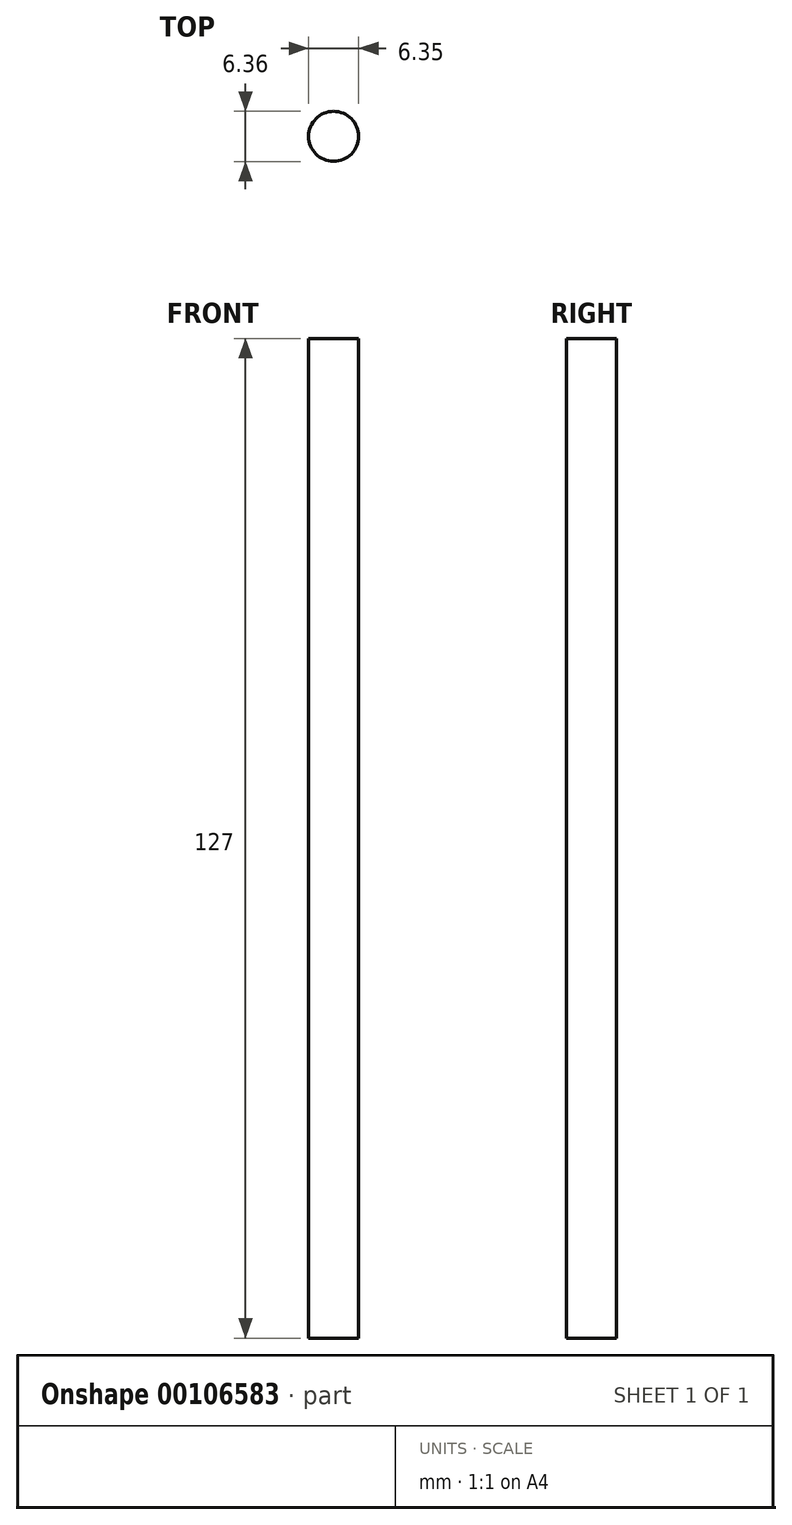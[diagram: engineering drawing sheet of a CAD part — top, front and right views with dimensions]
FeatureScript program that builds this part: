
annotation { "Feature Type Name" : "Feature", "Feature Type Description" : "" }
export const myFeature = defineFeature(function(context is Context, id is Id, definition is map)
    precondition{}
    {
        {
            var Q0;
            Q0=qCreatedBy(makeId("Front.planeOp"),FACE);
            var sketch = newSketch(context, id + "F0", { "sketchPlane" : qUnion([Q0])});
            skLineSegment(sketch, "E0.bottom", {"start": v(-24.08, 58.12) * mm, "end": v(-20.9, 58.12) * mm});
            skLineSegment(sketch, "E0.top", {"start": v(-24.08, -68.88) * mm, "end": v(-20.9, -68.88) * mm});
            skLineSegment(sketch, "E0.left", {"start": v(-24.08, 58.12) * mm, "end": v(-24.08, -68.88) * mm});
            skLineSegment(sketch, "E0.right", {"start": v(-20.9, 58.12) * mm, "end": v(-20.9, -68.88) * mm});
            skSolve(sketch);
        }
        {
            var Q0;
            Q0=makeQuery(id+"F0.imprint","IMPRINT",FACE,{"disambiguationData":[TD([[makeQuery(id+"F0.imprint","IMPRINT",EDGE,{"derivedFrom":sQuery(id+"F0.wireOp",EDGE,"E0.bottom")}),-1.0]])]});
            var Q1;
            Q1=sQuery(id+"F0.wireOp",EDGE,"E0.left");
            revolve(context, id + "F1", {"entities" : qUnion([Q0]), "axis" : qUnion([Q1]), "revolveType" : RevolveType.FULL});
        }
    });
